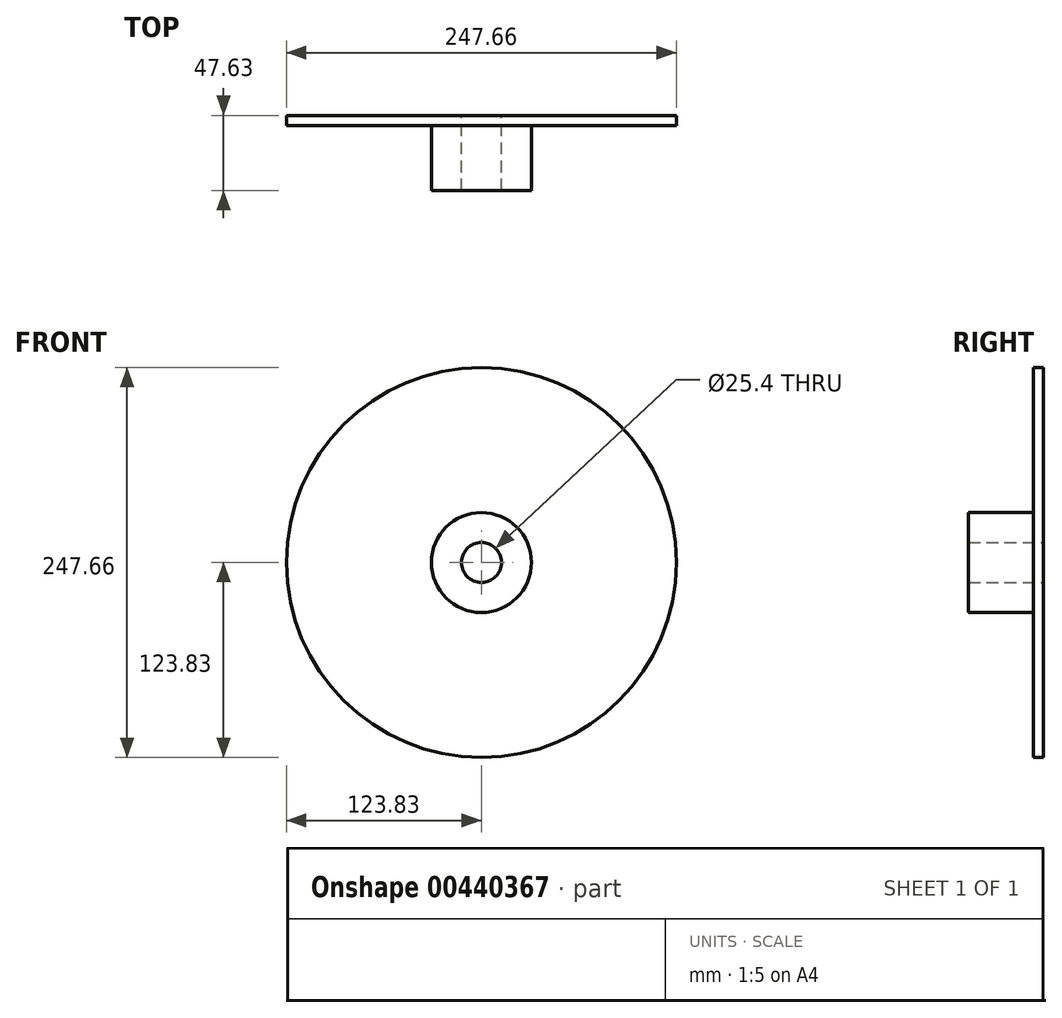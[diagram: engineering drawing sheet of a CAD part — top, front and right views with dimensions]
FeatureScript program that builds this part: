
annotation { "Feature Type Name" : "Feature", "Feature Type Description" : "" }
export const myFeature = defineFeature(function(context is Context, id is Id, definition is map)
    precondition{}
    {
        {
            var Q0;
            Q0=qCreatedBy(makeId("Front.planeOp"),FACE);
            var sketch = newSketch(context, id + "F0", { "sketchPlane" : qUnion([Q0])});
            skCircle(sketch, "E0", {"center": v(0, 0) * mm, "radius": 127 * mm});
            skCircle(sketch, "E1", {"center": v(0, 0) * mm, "radius": 31.75 * mm});
            skCircle(sketch, "E2", {"center": v(0, 0) * mm, "radius": 12.7 * mm});
            skSolve(sketch);
        }
        {
            var Q0;
            Q0=makeQuery(id+"F0.imprint","IMPRINT",FACE,{"disambiguationData":[TD([[makeQuery(id+"F0.imprint","IMPRINT",EDGE,{"derivedFrom":sQuery(id+"F0.wireOp",EDGE,"E1")}),1.0]])]});
            extrude(context, id + "F1", {"entities" : qUnion([Q0]), "depth" : 44.45 * mm});
        }
        {
            var Q0;
            Q0=qCreatedBy(makeId("Front.planeOp"),FACE);
            var sketch = newSketch(context, id + "F2", { "sketchPlane" : qUnion([Q0])});
            skCircle(sketch, "E3", {"center": v(0, 0) * mm, "radius": 127 * mm});
            skSolve(sketch);
        }
        {
            var Q0;
            Q0=makeQuery(id+"F2.imprint","IMPRINT",FACE,{"disambiguationData":[TD([[makeQuery(id+"F2.imprint","IMPRINT",EDGE,{"derivedFrom":sQuery(id+"F2.wireOp",EDGE,"E3")}),1.0]])]});
            extrude(context, id + "F3", {"entities" : qUnion([Q0]), "operationType" : NewBodyOperationType.ADD, "endBound" : BoundingType.SYMMETRIC, "depth" : 6.35 * mm});
        }
        {
            var Q0;
            Q0=makeQuery(id+"F3.boolean.opBoolean","SPLIT",FACE,{"disambiguationData":[TD([makeQuery(id+"F1.opExtrude","SWEPT_FACE",FACE,{"disambiguationData":[OSD([sQuery(id+"F0.wireOp",EDGE,"E2")])]})])],"derivedFrom":makeQuery(id+"F3.opExtrude","CAP_FACE",FACE,{"disambiguationData":[OSD([sQuery(id+"F2.wireOp",EDGE,"E3")])],"isStart":false})});
            var sketch = newSketch(context, id + "F4", { "sketchPlane" : qUnion([Q0])});
            skSolve(sketch);
        }
        {
            var Q0;
            Q0=makeQuery(id+"F4.imprint","IMPRINT",FACE,{"disambiguationData":[TD([[makeQuery(id+"F4.imprint","IMPRINT",EDGE,{"derivedFrom":makeQuery(id+"F3.boolean.opBoolean","INTERSECT",EDGE,{"derivedFrom":[makeQuery(id+"F1.opExtrude","SWEPT_FACE",FACE,{"disambiguationData":[OSD([sQuery(id+"F0.wireOp",EDGE,"E2")])]}),makeQuery(id+"F3.opExtrude","CAP_FACE",FACE,{"disambiguationData":[OSD([sQuery(id+"F2.wireOp",EDGE,"E3")])],"isStart":false})]})}),1.0]])]});
            extrude(context, id + "F5", {"entities" : qUnion([Q0]), "operationType" : NewBodyOperationType.REMOVE, "endBound" : BoundingType.SYMMETRIC, "oppositeDirection" : true, "depth" : 76.2 * mm});
        }
        {
            var Q0;
            {var subQ0=sQuery(id+"F2.wireOp",EDGE,"E3");Q0=makeQuery(id+"F3.boolean.opBoolean","SPLIT",FACE,{"disambiguationData":[TD([makeQuery(id+"F1.opExtrude","SWEPT_FACE",FACE,{"disambiguationData":[OSD([sQuery(id+"F0.wireOp",EDGE,"E1")])]})])],"derivedFrom":makeQuery(id+"F3.opExtrude","CAP_FACE",FACE,{"disambiguationData":[OSD([subQ0])],"isStart":false})});}
            var sketch = newSketch(context, id + "F6", { "sketchPlane" : qUnion([Q0])});
            skCircle(sketch, "E4", {"center": v(0, 0) * mm, "radius": 123.83 * mm});
            skSolve(sketch);
        }
        {
            var Q0;
            Q0=makeQuery(id+"F6.imprint","IMPRINT",FACE,{"disambiguationData":[TD([[makeQuery(id+"F6.imprint","IMPRINT",EDGE,{"derivedFrom":sQuery(id+"F6.wireOp",EDGE,"E4")}),-1.0]])]});
            extrude(context, id + "F7", {"entities" : qUnion([Q0]), "operationType" : NewBodyOperationType.REMOVE, "endBound" : BoundingType.SYMMETRIC, "depth" : 25.4 * mm});
        }
    });
